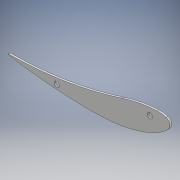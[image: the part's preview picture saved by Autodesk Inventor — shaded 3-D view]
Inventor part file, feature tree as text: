
AUTODESK INVENTOR PART (.ipt)
format: ipt  version: 2018.2 (Build 222227000, 227)  size: 134,656 bytes
history: native  units: mm
features: extrude x2, sketch x2, other x1, projected_geometry x1
ambient origin geometry x8: Origin, YZ Plane, XZ Plane, XY Plane, X Axis, Y Axis, Z Axis, Center Point
bodies: Body1 (feature_tree)
feature tree (6):
  extrude  "押し出し1"  Depth=4.0mm TaperAngle=0.0deg
  extrude  "押し出し2"  Depth=290.0mm
  other  "厚み1"
  sketch  "スケッチ1"
  projected_geometry  "投影ループ1"
  sketch  "スケッチ2"
